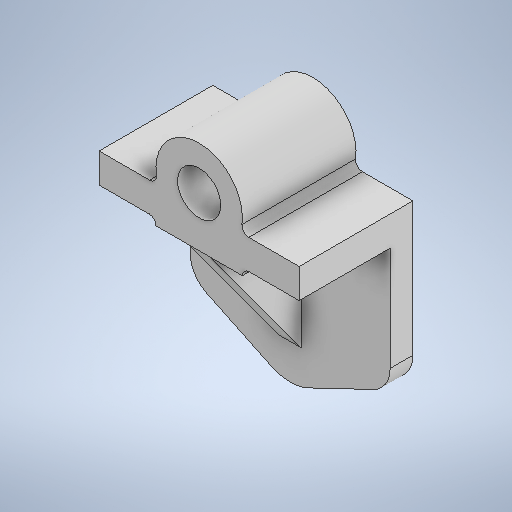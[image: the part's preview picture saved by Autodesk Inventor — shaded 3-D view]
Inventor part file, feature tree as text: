
AUTODESK INVENTOR PART (.ipt)
format: ipt  version: 2025.2 (Build 292293000, 293)  size: 1,845,760 bytes
history: native  units: in
note: dims shown in document units (in); Inventor stores cm internally (conversion verified against a paired STEP export)
features: sketch x7, extrude x5, plane x2, fillet x2, other x2, rib x1
ambient origin geometry x8: Origin, YZ Plane, XZ Plane, XY Plane, X Axis, Y Axis, Z Axis, Center Point
bodies: Solid1 (feature_tree)
feature tree (19):
  extrude  "Extrusion1"  Depth=3.4646in
  extrude  "Extrusion2"  Depth=0.5118in
  sketch  "Sketch3"  dims[d10=0.3937in d11=0.0in d12=0.5118in]
  plane  "Work Plane1"
  rib  "Rib1"
  extrude  "Extrusion3"  Depth=0.5118in
  fillet  "Face Fillet1"
  fillet  "Face Fillet2"
  plane  "Work Plane2"
  extrude  "Extrusion4"  Depth=1.5748in
  extrude  "Extrusion5"  Depth=0.3937in
  sketch  "Sketch1"  dims[d5=3.4646in d6=2.6378in]
  other  "Image1"
  sketch  "Sketch2"  dims[d7=1.4961in d9=0.5118in]
  sketch  "Sketch4"  dims[d13=1.5748in d14=0.0in d15=0.0394in]
  sketch  "Sketch5"  dims[d16=0.3937in d17=0.0in d18=0.0in d19=0.0394in d20=0.0394in d21=0.5512in]
  sketch  "Sketch6"  dims[d22=0.5512in]
  other  "Image2"
  sketch  "Sketch7"  dims[d23=0.1181in d24=0.0in d25=0.1181in d26=0.1181in d27=1.9685in d33=0.748in d34=1.4961in d36=0.748in d37=0.1181in d38=1.9685in d39=0.0in d40=0.748in d41=1.9685in d42=0.0in d43=0.1181in]
